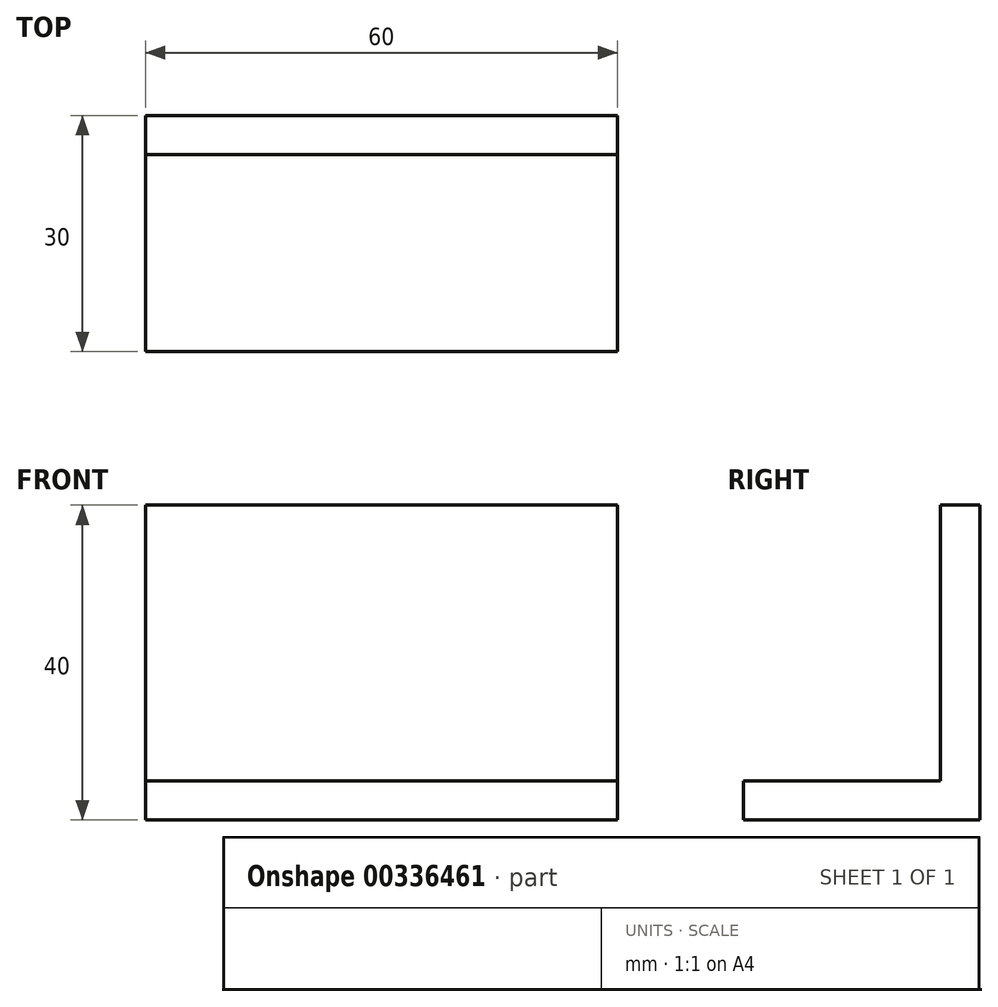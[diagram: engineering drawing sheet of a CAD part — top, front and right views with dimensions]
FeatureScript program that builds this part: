
annotation { "Feature Type Name" : "Feature", "Feature Type Description" : "" }
export const myFeature = defineFeature(function(context is Context, id is Id, definition is map)
    precondition{}
    {
        {
            var Q0;
            Q0=qCreatedBy(makeId("Right.planeOp"),FACE);
            var sketch = newSketch(context, id + "F0", { "sketchPlane" : qUnion([Q0])});
            skLineSegment(sketch, "E0", {"start": v(0, 40) * mm, "end": v(0, 0) * mm});
            skLineSegment(sketch, "E1", {"start": v(0, 0) * mm, "end": v(-30, 0) * mm});
            skLineSegment(sketch, "E2", {"start": v(-30, 0) * mm, "end": v(-30, 5) * mm});
            skLineSegment(sketch, "E3", {"start": v(-30, 5) * mm, "end": v(-4.98, 5) * mm});
            skLineSegment(sketch, "E4", {"start": v(-4.98, 5) * mm, "end": v(-4.98, 40) * mm});
            skLineSegment(sketch, "E5", {"start": v(-4.98, 40) * mm, "end": v(0, 40) * mm});
            skPoint(sketch, "E6.orphan", {"position": v(0, 43.14) * mm});
            skSolve(sketch);
        }
        {
            var Q0;
            Q0=makeQuery(id+"F0.imprint","IMPRINT",FACE,{"disambiguationData":[TD([[makeQuery(id+"F0.imprint","IMPRINT",EDGE,{"derivedFrom":sQuery(id+"F0.wireOp",EDGE,"E0")}),-1.0]])]});
            extrude(context, id + "F1", {"entities" : qUnion([Q0]), "endBound" : BoundingType.SYMMETRIC, "depth" : 60 * mm});
        }
    });
